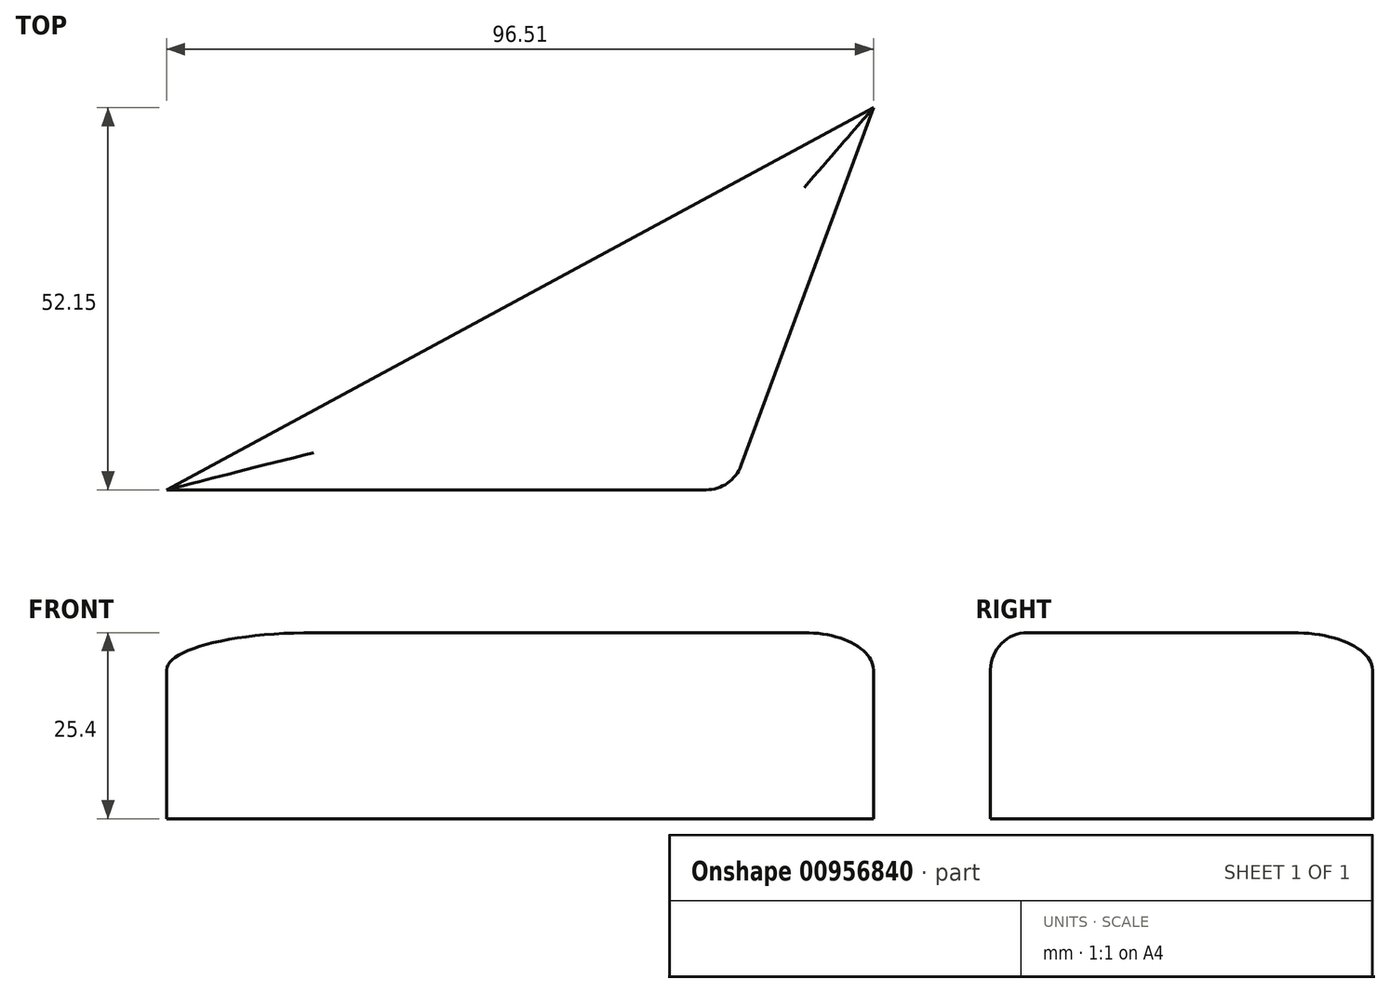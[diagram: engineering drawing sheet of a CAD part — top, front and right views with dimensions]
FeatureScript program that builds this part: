
annotation { "Feature Type Name" : "Feature", "Feature Type Description" : "" }
export const myFeature = defineFeature(function(context is Context, id is Id, definition is map)
    precondition{}
    {
        {
            var Q0;
            Q0=qCreatedBy(makeId("Top.planeOp"),FACE);
            var sketch = newSketch(context, id + "F0", { "sketchPlane" : qUnion([Q0])});
            skLineSegment(sketch, "E0", {"start": v(-43.86, -18.63) * mm, "end": v(33.35, -18.63) * mm});
            skLineSegment(sketch, "E1", {"start": v(33.35, -18.63) * mm, "end": v(52.65, 33.52) * mm});
            skLineSegment(sketch, "E2", {"start": v(-43.86, -18.63) * mm, "end": v(52.65, 33.52) * mm});
            skSolve(sketch);
        }
        {
            var Q0;
            Q0 = qSketchRegion(id + "F0", true);
            extrude(context, id + "F1", {"entities" : qUnion([Q0]), "depth" : 25.4 * mm, "offsetDistance" : 25.4 * mm});
        }
        {
            var Q0;
            Q0=makeQuery(id+"F1.opExtrude","SWEPT_EDGE",EDGE,{"disambiguationData":[OSD([sQuery(id+"F0.wireOp",EDGE,"E0"),sQuery(id+"F0.wireOp",EDGE,"E1")])]});
            fillet(context, id + "F2", {"entities" : qUnion([Q0]), "radius" : 5.08 * mm, "tangentPropagation" : true, "allowEdgeOverflow" : false});
        }
        {
            var Q0;
            Q0=makeQuery(id+"F1.opExtrude","CAP_FACE",FACE,{"disambiguationData":[OSD([sQuery(id+"F0.wireOp",EDGE,"E0"),sQuery(id+"F0.wireOp",EDGE,"E1"),sQuery(id+"F0.wireOp",EDGE,"E2")])],"isStart":false});
            fillet(context, id + "F3", {"entities" : qUnion([Q0]), "radius" : 5.08 * mm, "tangentPropagation" : true, "allowEdgeOverflow" : false});
        }
    });
